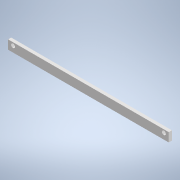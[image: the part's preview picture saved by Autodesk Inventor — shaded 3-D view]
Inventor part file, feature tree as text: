
AUTODESK INVENTOR PART (.ipt)
format: ipt  version: 2022 (Build 260153000, 153)  size: 108,032 bytes
history: native  units: mm
features: reference x11, other x3, extrude x1, sketch x1
ambient origin geometry x8: Origin, YZ Plane, XZ Plane, XY Plane, X Axis, Y Axis, Z Axis, Center Point
bodies: Solid1 (feature_tree)
feature tree (16):
  extrude  "Extrusion1"  Depth=9.0mm
  sketch  "Sketch1"  dims[d0=162.0mm d1=9.0mm d2=4.0mm d3=3.7mm d5=3.2mm d6=0.0mm]
  reference  "Reference1"
  reference  "Reference2"
  reference  "Reference3"
  reference  "Reference4"
  reference  "Reference5"
  reference  "Reference6"
  reference  "Reference7"
  reference  "Reference8"
  reference  "Reference9"
  reference  "Reference10"
  reference  "Reference11"
  other  "Caja_Reductora.iam"
  other  "Carcasa_CajaR_Lateral1:1"
  other  "Rodamiento_Ejes:8"
